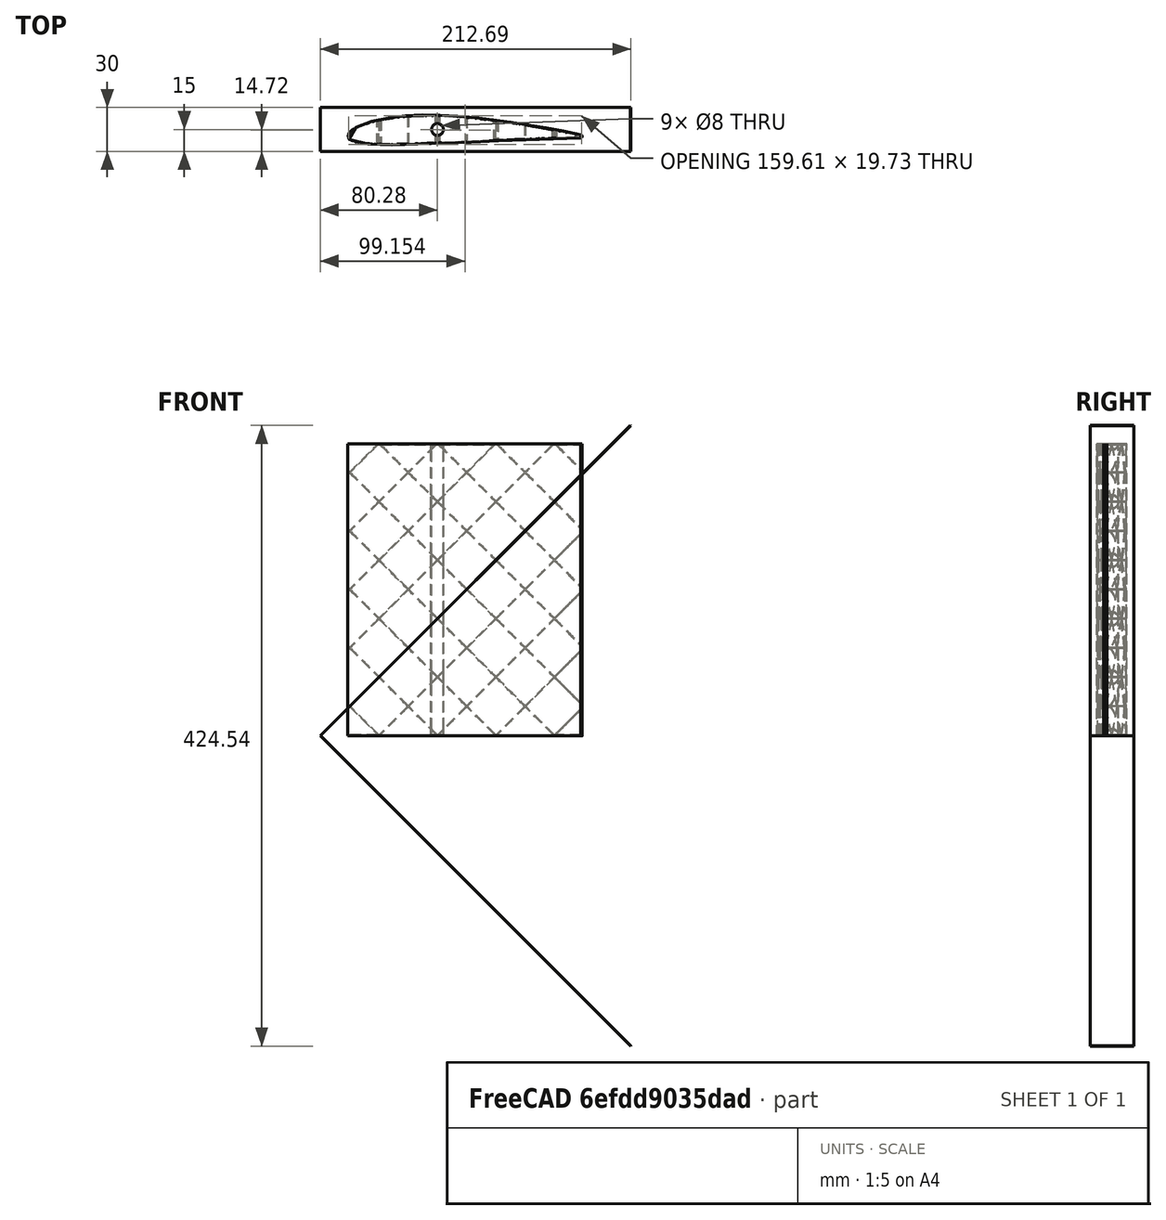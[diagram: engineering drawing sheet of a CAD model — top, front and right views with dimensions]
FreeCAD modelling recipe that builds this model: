
FCSTD DOCUMENT  (FreeCAD 0.21R33771 (Git))
Label: wing_v1
License: All rights reserved
LicenseURL: https://en.wikipedia.org/wiki/All_rights_reserved
objects: PartDesign::Body×6, Sketcher::SketchObject×5, PartDesign::Pad×5, Part::MultiFuse×5, Part::Cylinder×4, Part::FeaturePython×3, Part::Cut×3, PartDesign::Thickness×2, Part::Box×2, Part::MultiCommon×2, Image::ImagePlane×1, PartDesign::FeatureBase×1
note: 42 computed .brp shape members not serialized (recipe doc carries the construction recipe); baked Part::Feature solids carry a one-line shape summary decoded from their .brp

FEATURE [Image::ImagePlane] Screenshot_from_2023_09_17_14_32_16  label="Screenshot from 2023-09-17 14-32-16"
  XSize = 164.233
  YSize = 29.0321
FEATURE [Sketcher::SketchObject] Sketch
  FullyConstrained = false
  MapMode = 5
  Support = -> [XY_Plane]
  sketch-geometry (30):
    g0: ArcOfCircle CenterX=78.0455 CenterY=-4.69261 CenterZ=0 NormalX=0 NormalY=0 NormalZ=1 AngleXU=0 Radius=0.633228 StartAngle=4.68069 EndAngle=7.80443
    g1-g15: Circle x15 (B-spline internal-alignment scaffolding for g16; pole/knot coordinates omitted)
    g16: BSplineCurve PolesCount=15 KnotsCount=13 Degree=3 IsPeriodic=0
    g17-g29: GeomPoint x13 (B-spline internal-alignment scaffolding for g16; pole/knot coordinates omitted)
  constraints (6):
    c: Weight(g1) = 1
    c: Coincident(g16,g0)
    c: Equal(g1, g2-g15) x14
    c: Coincident(g16,g0)
    c: InternalAlignment(g1-g15 -> g16) x15
    c: InternalAlignment(g17-g29 -> g16) x13
FEATURE [PartDesign::Pad] Pad
  Direction = (0,0,1)
  Length = 200
  Length2 = 10
  Profile = -> Sketch
  Type = 0
FEATURE [Sketcher::SketchObject] Sketch001
  FullyConstrained = false
  MapMode = 5
  Support = -> [XY_Plane001]
  sketch-geometry (30):
    g0: ArcOfCircle CenterX=78.0455 CenterY=-4.69261 CenterZ=0 NormalX=0 NormalY=0 NormalZ=1 AngleXU=0 Radius=0.633228 StartAngle=4.68069 EndAngle=7.80443
    g1-g15: Circle x15 (B-spline internal-alignment scaffolding for g16; pole/knot coordinates omitted)
    g16: BSplineCurve PolesCount=15 KnotsCount=13 Degree=3 IsPeriodic=0
    g17-g29: GeomPoint x13 (B-spline internal-alignment scaffolding for g16; pole/knot coordinates omitted)
  constraints (6):
    c: Weight(g1) = 1
    c: Coincident(g16,g0)
    c: Equal(g1, g2-g15) x14
    c: Coincident(g16,g0)
    c: InternalAlignment(g1-g15 -> g16) x15
    c: InternalAlignment(g17-g29 -> g16) x13
FEATURE [PartDesign::Pad] Pad001
  Direction = (0,0,1)
  Length = 200
  Length2 = 10
  Profile = -> Sketch001
  Type = 0
FEATURE [PartDesign::Body] Body001
  Group = -> [Sketch001,Pad001]
  Origin = -> Origin001
  Tip = -> Pad001
FEATURE [PartDesign::Thickness] Thickness
  Base = -> Pad [Face4,Face3]
  BaseFeature = -> Pad
  Intersection = false
  Join = 0
  Mode = 1
  SupportTransform = false
  Value = 0.4
FEATURE [PartDesign::Body] Body
  Group = -> [Sketch,Pad,Thickness]
  Origin = -> Origin
  Tip = -> Thickness
FEATURE [Part::Box] Box  label="Cube"
  AttacherType = Attacher::AttachEngine3D
  Height = 0.4
  Length = 300
  Placement = pos=(-100,-15,0) rot=(0,1,0;0.785398rad)
  Width = 30
FEATURE [Part::FeaturePython] Array  # Draft array (typed FeaturePython)
  AlwaysSyncPlacement = false
  Angle = 360
  ArrayType = 0
  Axis = (0,0,1)
  Base = -> Box
  Center = (0,0,0)
  Count = 10
  ExpandArray = false
  Fuse = false
  IntervalAxis = (0,0,0)
  IntervalX = (100,0,0)
  IntervalY = (0,100,0)
  IntervalZ = (0,0,40)
  NumberCircles = 3
  NumberPolar = 5
  NumberX = 1
  NumberY = 1
  NumberZ = 10
  PlacementList = 10 placements: arithmetic series from (-100,-15,0) step (0,0,40) to (-100,-15,360)
  RadialDistance = 50
  ScaleList = (10) [(1,1,1),(1,1,1),(1,1,1),(1,1,1),(1,1,1),(1,1,1),(1,1,1),(1,1,1),(1,1,1),(1,1,1)]
  Symmetry = 1
  TangentialDistance = 25
FEATURE [Part::Box] Box001  label="Cube001"
  AttacherType = Attacher::AttachEngine3D
  Height = 0.4
  Length = 300
  Placement = pos=(-100,-15,0) rot=(0,-1,0;0.785398rad)
  Width = 30
FEATURE [Part::FeaturePython] Array001  # Draft array (typed FeaturePython)
  AlwaysSyncPlacement = false
  Angle = 360
  ArrayType = 0
  Axis = (0,0,1)
  Base = -> Array
  Center = (0,0,0)
  Count = 9
  ExpandArray = false
  Fuse = false
  IntervalAxis = (0,0,0)
  IntervalX = (100,0,0)
  IntervalY = (0,100,0)
  IntervalZ = (0,0,40)
  NumberCircles = 3
  NumberPolar = 5
  NumberX = 1
  NumberY = 1
  NumberZ = 9
  PlacementList = 9 placements: arithmetic series from (0,0,0) step (0,0,40) to (0,0,320)
  RadialDistance = 50
  ScaleList = (9) [(1,1,1),(1,1,1),(1,1,1),(1,1,1),(1,1,1),(1,1,1),(1,1,1),(1,1,1),(1,1,1)]
  Symmetry = 1
  TangentialDistance = 25
FEATURE [Part::FeaturePython] Array002  # Draft array (typed FeaturePython)
  AlwaysSyncPlacement = false
  Angle = 360
  ArrayType = 0
  Axis = (0,0,1)
  Base = -> Box001
  Center = (0,0,0)
  Count = 20
  ExpandArray = false
  Fuse = false
  IntervalAxis = (0,0,0)
  IntervalX = (100,0,0)
  IntervalY = (0,100,0)
  IntervalZ = (0,0,40)
  NumberCircles = 3
  NumberPolar = 5
  NumberX = 1
  NumberY = 1
  NumberZ = 20
  Placement = pos=(0,1.90735e-05,-160) rot=(0,0,1;0rad)
  PlacementList = 20 placements: arithmetic series from (-100,-15,0) step (0,0,40) to (-100,-15,760)
  RadialDistance = 50
  ScaleList = (20) [(1,1,1),(1,1,1),(1,1,1),(1,1,1),(1,1,1),(1,1,1),(1,1,1),(1,1,1),(1,1,1),(1,1,1),(1,1,1),(1,1,1),(1,1,1),(1,1,1),(1,1,1),(1,1,1),(1,1,1),(1,1,1),(1,1,1),(1,1,1)]
  Symmetry = 1
  TangentialDistance = 25
FEATURE [Sketcher::SketchObject] Sketch002
  FullyConstrained = false
  MapMode = 5
  Support = -> [XY_Plane002]
  sketch-geometry (30):
    g0: ArcOfCircle CenterX=78.0455 CenterY=-4.69261 CenterZ=0 NormalX=0 NormalY=0 NormalZ=1 AngleXU=0 Radius=0.633228 StartAngle=4.68069 EndAngle=7.80443
    g1-g15: Circle x15 (B-spline internal-alignment scaffolding for g16; pole/knot coordinates omitted)
    g16: BSplineCurve PolesCount=15 KnotsCount=13 Degree=3 IsPeriodic=0
    g17-g29: GeomPoint x13 (B-spline internal-alignment scaffolding for g16; pole/knot coordinates omitted)
  constraints (6):
    c: Weight(g1) = 1
    c: Coincident(g16,g0)
    c: Equal(g1, g2-g15) x14
    c: Coincident(g16,g0)
    c: InternalAlignment(g1-g15 -> g16) x15
    c: InternalAlignment(g17-g29 -> g16) x13
FEATURE [PartDesign::Pad] Pad002
  Direction = (0,0,1)
  Length = 200
  Length2 = 10
  Profile = -> Sketch002
  Type = 0
FEATURE [PartDesign::Body] Body002
  Group = -> [Sketch002,Pad002]
  Origin = -> Origin002
  Tip = -> Pad002
FEATURE [Part::MultiCommon] Common
  Shapes = -> [Body002,Array002]
FEATURE [Part::MultiCommon] Common001
  Shapes = -> [Body001,Array001]
FEATURE [Part::MultiFuse] Fusion
  Shapes = -> [Common001,Common]
FEATURE [Part::MultiFuse] Fusion001
  Shapes = -> [Body,Fusion]
FEATURE [Part::Cylinder] Cylinder
  Angle = 360
  AttacherType = Attacher::AttachEngine3D
  FirstAngle = 0
  Height = 200
  Placement = pos=(-20,0,0) rot=(0,0,1;0rad)
  Radius = 4
  SecondAngle = 0
FEATURE [Part::Cut] Cut
  Base = -> Fusion001
  Tool = -> Cylinder
FEATURE [Sketcher::SketchObject] Sketch003
  FullyConstrained = false
  MapMode = 5
  Support = -> [XY_Plane004]
  sketch-geometry (30):
    g0: ArcOfCircle CenterX=78.0455 CenterY=-4.69261 CenterZ=0 NormalX=0 NormalY=0 NormalZ=1 AngleXU=0 Radius=0.633228 StartAngle=4.68069 EndAngle=7.80443
    g1-g15: Circle x15 (B-spline internal-alignment scaffolding for g16; pole/knot coordinates omitted)
    g16: BSplineCurve PolesCount=15 KnotsCount=13 Degree=3 IsPeriodic=0
    g17-g29: GeomPoint x13 (B-spline internal-alignment scaffolding for g16; pole/knot coordinates omitted)
  constraints (6):
    c: Weight(g1) = 1
    c: Coincident(g16,g0)
    c: Equal(g1, g2-g15) x14
    c: Coincident(g16,g0)
    c: InternalAlignment(g1-g15 -> g16) x15
    c: InternalAlignment(g17-g29 -> g16) x13
FEATURE [PartDesign::Pad] Pad003
  Direction = (1,1,1)
  Length = 0.8
  Length2 = 100
  Profile = -> Sketch003
  Type = 0
FEATURE [PartDesign::Body] Body004
  Group = -> [Sketch003,Pad003]
  Origin = -> Origin004
  Tip = -> Pad003
FEATURE [Part::Cylinder] Cylinder001
  Angle = 360
  AttacherType = Attacher::AttachEngine3D
  FirstAngle = 0
  Height = 200
  Placement = pos=(-20,0,0) rot=(0,0,1;0rad)
  Radius = 4
  SecondAngle = 0
FEATURE [Part::Cut] Cut001
  Base = -> Body004
  Tool = -> Cylinder001
FEATURE [Part::Cylinder] Cylinder002
  Angle = 360
  AttacherType = Attacher::AttachEngine3D
  FirstAngle = 0
  Height = 200
  Placement = pos=(-20,0,0) rot=(0,0,1;0rad)
  Radius = 4
  SecondAngle = 0
FEATURE [Sketcher::SketchObject] Sketch004
  FullyConstrained = false
  MapMode = 5
  Support = -> [XY_Plane005]
  sketch-geometry (30):
    g0: ArcOfCircle CenterX=78.0455 CenterY=-4.69261 CenterZ=0 NormalX=0 NormalY=0 NormalZ=1 AngleXU=0 Radius=0.633228 StartAngle=4.68069 EndAngle=7.80443
    g1-g15: Circle x15 (B-spline internal-alignment scaffolding for g16; pole/knot coordinates omitted)
    g16: BSplineCurve PolesCount=15 KnotsCount=13 Degree=3 IsPeriodic=0
    g17-g29: GeomPoint x13 (B-spline internal-alignment scaffolding for g16; pole/knot coordinates omitted)
  constraints (6):
    c: Weight(g1) = 1
    c: Coincident(g16,g0)
    c: Equal(g1, g2-g15) x14
    c: Coincident(g16,g0)
    c: InternalAlignment(g1-g15 -> g16) x15
    c: InternalAlignment(g17-g29 -> g16) x13
FEATURE [PartDesign::Pad] Pad004
  Direction = (1,1,1)
  Length = 0.8
  Length2 = 100
  Profile = -> Sketch004
  Type = 0
FEATURE [PartDesign::Body] Body005
  Group = -> [Sketch004,Pad004]
  Origin = -> Origin005
  Tip = -> Pad004
FEATURE [Part::Cut] Cut002
  Base = -> Body005
  Placement = pos=(0,0,199.2) rot=(0,0,1;0rad)
  Tool = -> Cylinder002
FEATURE [Part::Cylinder] Cylinder003
  Angle = 360
  AttacherType = Attacher::AttachEngine3D
  FirstAngle = 0
  Height = 200
  Placement = pos=(-20,0,0) rot=(0,0,1;0rad)
  Radius = 4
  SecondAngle = 0
FEATURE [PartDesign::FeatureBase] BaseFeature
  BaseFeature = -> Cylinder003
FEATURE [PartDesign::Thickness] Thickness001
  Base = -> BaseFeature [Face3,Face2]
  BaseFeature = -> BaseFeature
  Intersection = false
  Join = 0
  Mode = 1
  SupportTransform = false
  Value = 0.4
FEATURE [PartDesign::Body] Body003
  BaseFeature = -> Cylinder003
  Group = -> [BaseFeature,Thickness001]
  Origin = -> Origin003
  Placement = pos=(-20,0,0) rot=(0,0,1;0rad)
  Tip = -> Thickness001
FEATURE [Part::MultiFuse] Fusion002
  Shapes = -> [Body003,Cut]
FEATURE [Part::MultiFuse] Fusion003
  Shapes = -> [Fusion002,Cut002]
FEATURE [Part::MultiFuse] Fusion004
  Shapes = -> [Cut001,Fusion003]
